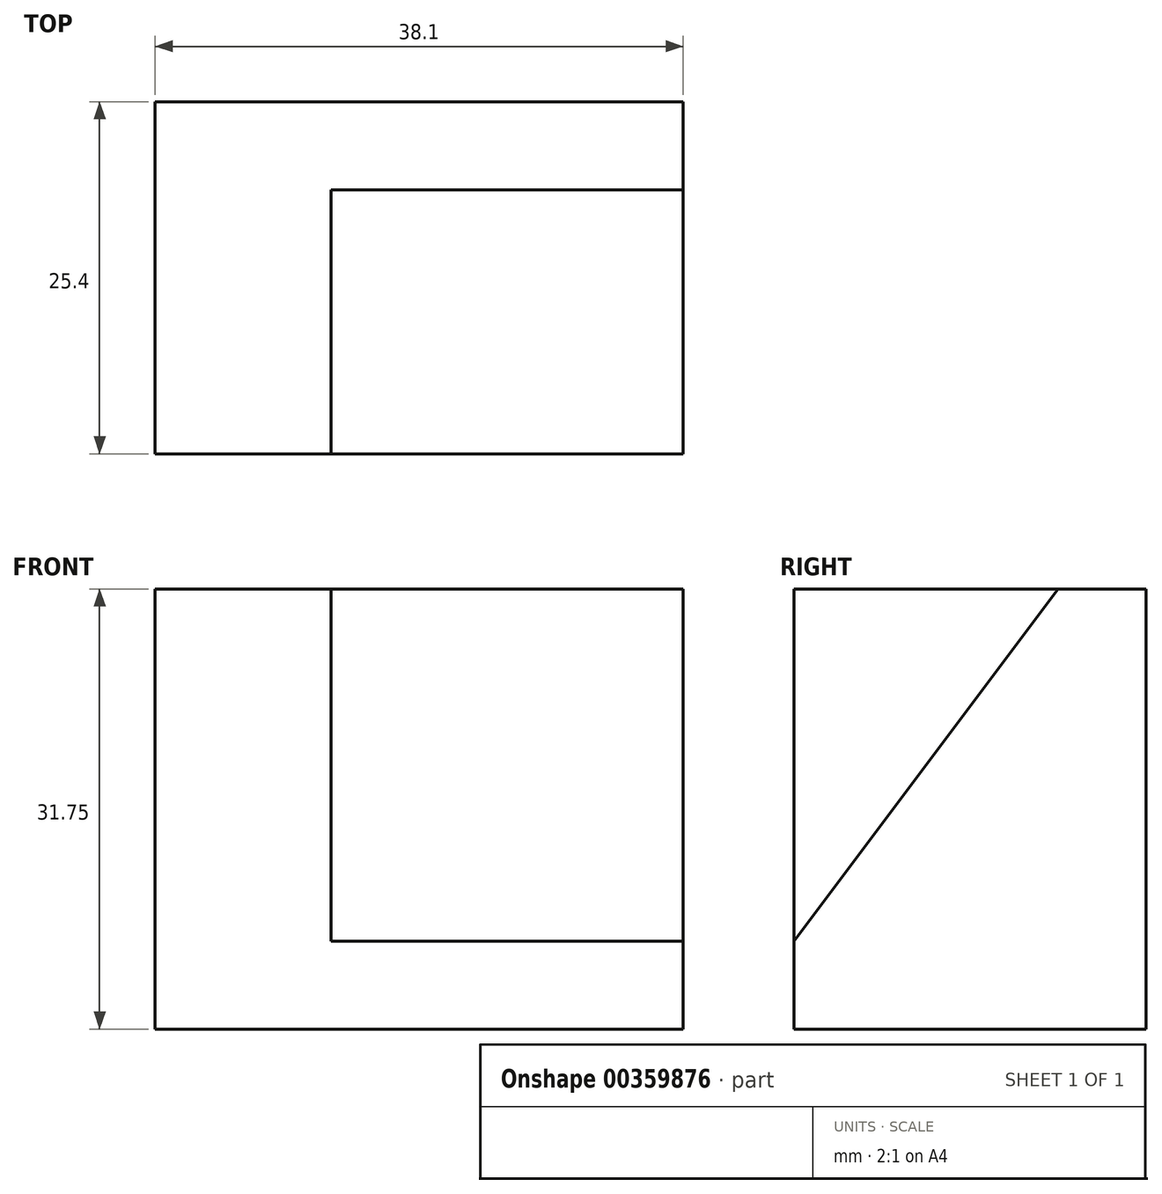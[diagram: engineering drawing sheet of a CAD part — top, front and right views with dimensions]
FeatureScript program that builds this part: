
annotation { "Feature Type Name" : "Feature", "Feature Type Description" : "" }
export const myFeature = defineFeature(function(context is Context, id is Id, definition is map)
    precondition{}
    {
        {
            var Q0;
            Q0=qCreatedBy(makeId("Right.planeOp"),FACE);
            var sketch = newSketch(context, id + "F0", { "sketchPlane" : qUnion([Q0])});
            skLineSegment(sketch, "E0", {"start": v(0, 0) * mm, "end": v(25.4, 0) * mm});
            skLineSegment(sketch, "E1", {"start": v(25.4, 0) * mm, "end": v(25.4, 31.75) * mm});
            skLineSegment(sketch, "E2", {"start": v(25.4, 31.75) * mm, "end": v(0, 31.75) * mm});
            skLineSegment(sketch, "E3", {"start": v(0, 31.75) * mm, "end": v(0, 0) * mm});
            skSolve(sketch);
        }
        {
            var Q0;
            Q0 = qSketchRegion(id + "F0", true);
            extrude(context, id + "F1", {"entities" : qUnion([Q0]), "depth" : 38.1 * mm});
        }
        {
            var Q0;
            Q0=makeQuery(id+"F1.opExtrude","CAP_FACE",FACE,{"disambiguationData":[OSD([sQuery(id+"F0.wireOp",EDGE,"E0"),sQuery(id+"F0.wireOp",EDGE,"E1"),sQuery(id+"F0.wireOp",EDGE,"E2"),sQuery(id+"F0.wireOp",EDGE,"E3")])],"isStart":false});
            var sketch = newSketch(context, id + "F2", { "sketchPlane" : qUnion([Q0])});
            skLineSegment(sketch, "E4", {"start": v(19.05, 31.75) * mm, "end": v(0, 6.35) * mm});
            skSolve(sketch);
        }
        {
            var Q0;
            {var subQ0=sQuery(id+"F2.wireOp",EDGE,"E4");Q0=makeQuery(id+"F2.imprint","IMPRINT",FACE,{"disambiguationData":[TD([[makeQuery(id+"F2.imprint","IMPRINT",EDGE,{"derivedFrom":subQ0}),-1.0]])]});}
            extrude(context, id + "F3", {"entities" : qUnion([Q0]), "operationType" : NewBodyOperationType.REMOVE, "oppositeDirection" : true, "depth" : 25.4 * mm});
        }
    });
